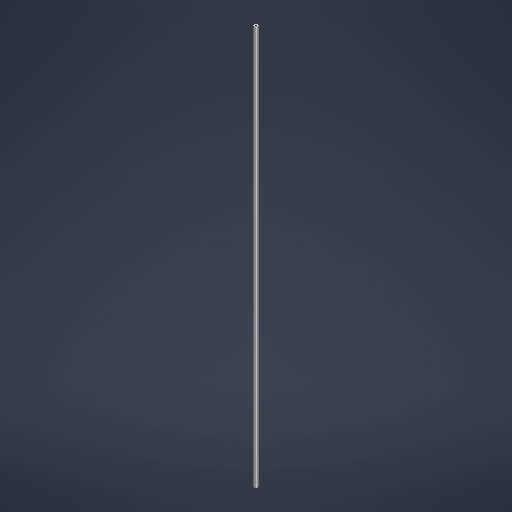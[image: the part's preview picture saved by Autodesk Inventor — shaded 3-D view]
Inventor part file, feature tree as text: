
AUTODESK INVENTOR PART (.ipt)
format: ipt  version: 2023 (Build 270158000, 158)  size: 739,328 bytes
history: native  units: in
note: dims shown in document units (in); Inventor stores cm internally (conversion verified against a paired STEP export)
features: mirror x1
ambient origin geometry x8: Origin, YZ Plane, XZ Plane, XY Plane, X Axis, Y Axis, Z Axis, Center Point
bodies: Solid1 (feature_tree)
feature tree (1):
  mirror  "Mirror2"
